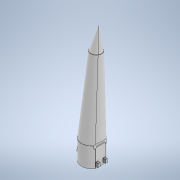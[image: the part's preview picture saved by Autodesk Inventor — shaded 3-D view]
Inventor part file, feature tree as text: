
AUTODESK INVENTOR PART (.ipt)
format: ipt  version: 2021 (Build 250183000, 183)  size: 646,656 bytes
history: native  units: mm
features: other x3, extrude x1, sketch x1
ambient origin geometry x8: Origin, YZ Plane, XZ Plane, XY Plane, X Axis, Y Axis, Z Axis, Center Point
bodies: Solid1 (feature_tree)
feature tree (5):
  other  "Soyuz Core Stage Part 1.ipt"
  extrude  "Extrusion1"  TaperAngle=0.0deg  [1 undecoded]
  other  "Soyuz Booster::Soyuz Core Stage Part 1.ipt"
  other  "TaggingFeature1"
  sketch  "Sketch1"  dims[d0=10.0mm d1=0.0mm d2=0.0mm d3=1.0mm d4=1.0mm d5=0.0mm]
note: 1 required parameter value undecoded (feature->parameter linkage not recoverable at this tier; creation-order binding heuristic only, values carry confidence <= 0.55)
